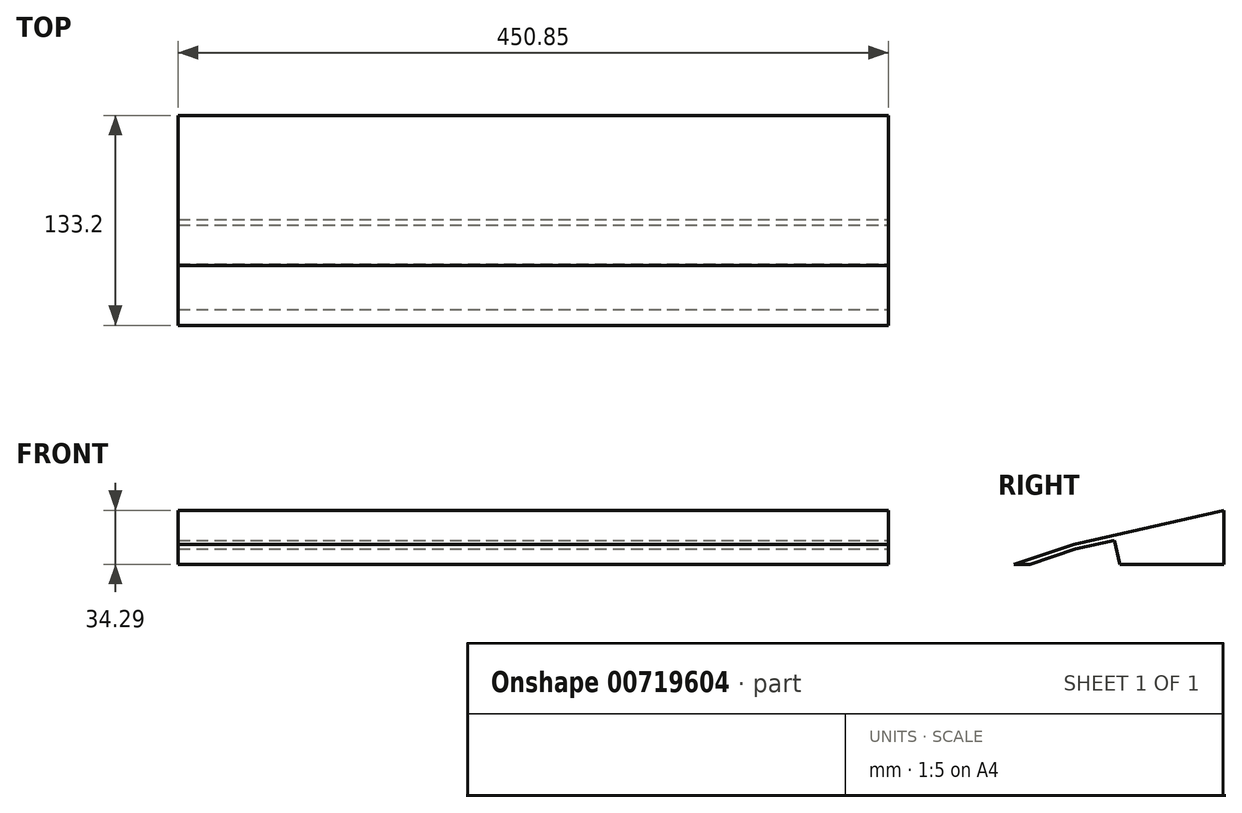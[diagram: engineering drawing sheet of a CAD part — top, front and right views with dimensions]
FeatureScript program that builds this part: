
annotation { "Feature Type Name" : "Feature", "Feature Type Description" : "" }
export const myFeature = defineFeature(function(context is Context, id is Id, definition is map)
    precondition{}
    {
        {
            var Q0;
            Q0=qCreatedBy(makeId("Right.planeOp"),FACE);
            var sketch = newSketch(context, id + "F0", { "sketchPlane" : qUnion([Q0])});
            skLineSegment(sketch, "E0", {"start": v(0, 0) * mm, "end": v(10.04, 0) * mm});
            skLineSegment(sketch, "E1", {"start": v(0, 0) * mm, "end": v(38.1, 12.7) * mm});
            skLineSegment(sketch, "E2", {"start": v(38.1, 12.7) * mm, "end": v(133.2, 34.3) * mm});
            skLineSegment(sketch, "E3", {"start": v(133.2, 34.3) * mm, "end": v(133.2, 0) * mm});
            skLineSegment(sketch, "E4.0", {"start": v(38.96, 9.64) * mm, "end": v(133.2, 31.03) * mm});
            skLineSegment(sketch, "E4.1", {"start": v(10.04, 0) * mm, "end": v(38.96, 9.64) * mm});
            skLineSegment(sketch, "E5", {"start": v(63.73, 15.26) * mm, "end": v(67.2, 0) * mm});
            skLineSegment(sketch, "E6.trimOffspring", {"start": v(67.2, 0) * mm, "end": v(133.2, 0) * mm});
            skSolve(sketch);
        }
        {
            var Q0;
            {var subQ4=sQuery(id+"F0.wireOp",EDGE,"E5");Q0=makeQuery(id+"F0.imprint","IMPRINT",FACE,{"disambiguationData":[TD([[makeQuery(id+"F0.imprint","IMPRINT",EDGE,{"derivedFrom":subQ4}),1.0]])]});}
            var Q1;
            Q1=makeQuery(id+"F0.imprint","IMPRINT",FACE,{"disambiguationData":[TD([[makeQuery(id+"F0.imprint","IMPRINT",EDGE,{"derivedFrom":sQuery(id+"F0.wireOp",EDGE,"E0")}),1.0]])]});
            extrude(context, id + "F1", {"entities" : qUnion([Q0, Q1]), "oppositeDirection" : true, "depth" : 450.85 * mm, "offsetDistance" : 25.4 * mm});
        }
    });
